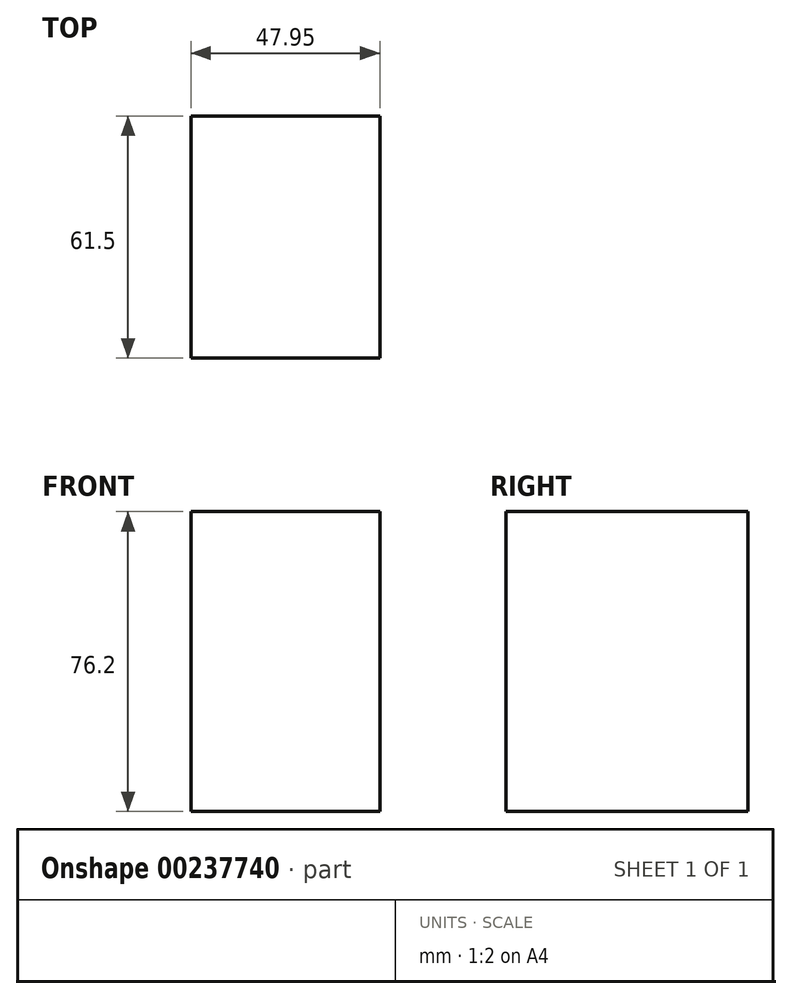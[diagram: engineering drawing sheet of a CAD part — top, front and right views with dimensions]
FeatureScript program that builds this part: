
annotation { "Feature Type Name" : "Feature", "Feature Type Description" : "" }
export const myFeature = defineFeature(function(context is Context, id is Id, definition is map)
    precondition{}
    {
        {
            var Q0;
            Q0=qCreatedBy(makeId("Top.planeOp"),FACE);
            var sketch = newSketch(context, id + "F0", { "sketchPlane" : qUnion([Q0])});
            skLineSegment(sketch, "E0.bottom", {"start": v(-48.7, 50.77) * mm, "end": v(-0.76, 50.77) * mm});
            skLineSegment(sketch, "E0.top", {"start": v(-48.7, 14.67) * mm, "end": v(-0.76, 14.67) * mm});
            skLineSegment(sketch, "E0.left", {"start": v(-48.7, 50.77) * mm, "end": v(-48.7, 14.67) * mm});
            skLineSegment(sketch, "E0.right", {"start": v(-0.76, 50.77) * mm, "end": v(-0.76, 14.67) * mm});
            skSolve(sketch);
        }
        {
            var Q0;
            Q0 = qSketchRegion(id + "F0", true);
            extrude(context, id + "F1", {"entities" : qUnion([Q0]), "oppositeDirection" : true, "depth" : 25.4 * mm});
        }
        {
            var Q0;
            Q0=makeQuery(id+"F1.opExtrude","SWEPT_FACE",FACE,{"disambiguationData":[OSD([sQuery(id+"F0.wireOp",EDGE,"E0.top")])]});
            extrude(context, id + "F2", {"entities" : qUnion([Q0]), "operationType" : NewBodyOperationType.ADD, "depth" : 25.4 * mm});
        }
        {
            var Q0;
            Q0=qCreatedBy(makeId("Top.planeOp"),FACE);
            var sketch = newSketch(context, id + "F3", { "sketchPlane" : qUnion([Q0])});
            skLineSegment(sketch, "E1", {"start": v(-47.66, 49.68) * mm, "end": v(0, -10.4) * mm});
            skLineSegment(sketch, "E2", {"start": v(-47.66, 27.15) * mm, "end": v(0, 27.15) * mm});
            skSolve(sketch);
        }
        {
            var Q0;
            Q0 = qSketchRegion(id + "F3", true);
            var Q1;
            {var subQ0=sQuery(id+"F0.wireOp",EDGE,"E0.top");Q1=makeQuery(id+"F2.boolean.opBoolean","MERGE",FACE,{"derivedFrom":[makeQuery(id+"F1.opExtrude","CAP_FACE",FACE,{"disambiguationData":[OSD([sQuery(id+"F0.wireOp",EDGE,"E0.bottom"),subQ0,sQuery(id+"F0.wireOp",EDGE,"E0.left"),sQuery(id+"F0.wireOp",EDGE,"E0.right")])],"isStart":true}),makeQuery(id+"F2.opExtrude","SWEPT_FACE",FACE,{"disambiguationData":[OSD([subQ0]),TDD([makeQuery(id+"F1.opExtrude","CAP_EDGE",EDGE,{"disambiguationData":[OSD([subQ0])],"isStart":true})])]})]});}
            extrude(context, id + "F4", {"entities" : qUnion([Q0, Q1]), "operationType" : NewBodyOperationType.ADD, "depth" : 50.8 * mm});
        }
    });
